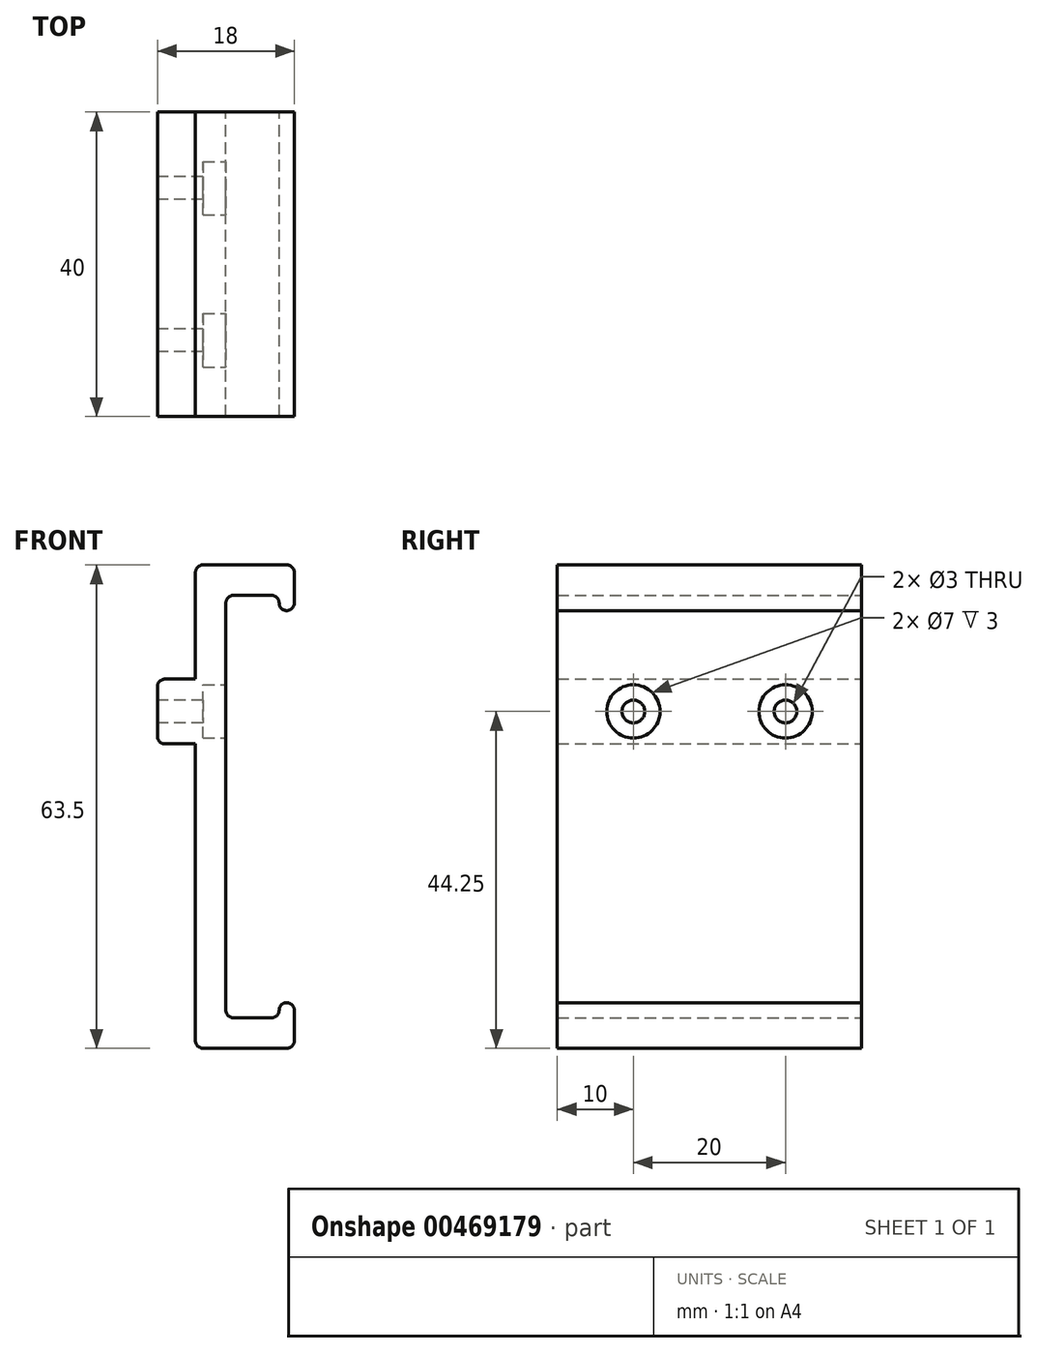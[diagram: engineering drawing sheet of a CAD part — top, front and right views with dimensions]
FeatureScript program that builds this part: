
annotation { "Feature Type Name" : "Feature", "Feature Type Description" : "" }
export const myFeature = defineFeature(function(context is Context, id is Id, definition is map)
    precondition{}
    {
        {
            var Q0;
            Q0=qCreatedBy(makeId("Front.planeOp"),FACE);
            var sketch = newSketch(context, id + "F0", { "sketchPlane" : qUnion([Q0])});
            skLineSegment(sketch, "E0", {"start": v(0, 15) * mm, "end": v(0, 0) * mm});
            skLineSegment(sketch, "E1", {"start": v(0, 0) * mm, "end": v(-5, 0) * mm});
            skLineSegment(sketch, "E2", {"start": v(-5, 0) * mm, "end": v(-5, -8.5) * mm});
            skLineSegment(sketch, "E3", {"start": v(-5, -8.5) * mm, "end": v(0, -8.5) * mm});
            skLineSegment(sketch, "E4", {"start": v(0, -8.5) * mm, "end": v(0, -48.5) * mm});
            skLineSegment(sketch, "E5", {"start": v(0, -48.5) * mm, "end": v(13, -48.5) * mm});
            skLineSegment(sketch, "E6", {"start": v(11, -44.5) * mm, "end": v(4, -44.5) * mm});
            skLineSegment(sketch, "E7", {"start": v(4, -44.5) * mm, "end": v(4, 11) * mm});
            skLineSegment(sketch, "E8", {"start": v(11, 11) * mm, "end": v(4, 11) * mm});
            skLineSegment(sketch, "E9", {"start": v(13, 15) * mm, "end": v(0, 15) * mm});
            skLineSegment(sketch, "E10", {"start": v(13, 9) * mm, "end": v(11, 9) * mm});
            skLineSegment(sketch, "E11", {"start": v(11, 9) * mm, "end": v(11, 11) * mm});
            skLineSegment(sketch, "E12", {"start": v(13, -42.5) * mm, "end": v(11, -42.5) * mm});
            skLineSegment(sketch, "E13", {"start": v(11, -42.5) * mm, "end": v(11, -44.5) * mm});
            skLineSegment(sketch, "E14", {"start": v(13, 15) * mm, "end": v(13, 9) * mm});
            skLineSegment(sketch, "E15", {"start": v(13, -48.5) * mm, "end": v(13, -42.5) * mm});
            skSolve(sketch);
        }
        {
            var Q0;
            Q0=makeQuery(id+"F0.imprint","IMPRINT",FACE,{"disambiguationData":[TD([[makeQuery(id+"F0.imprint","IMPRINT",EDGE,{"derivedFrom":sQuery(id+"F0.wireOp",EDGE,"E0")}),1.0]])]});
            extrude(context, id + "F1", {"entities" : qUnion([Q0]), "depth" : 40 * mm});
        }
        {
            var Q0;
            Q0=makeQuery(id+"F1.opExtrude","SWEPT_FACE",FACE,{"disambiguationData":[OSD([sQuery(id+"F0.wireOp",EDGE,"E2")])]});
            var sketch = newSketch(context, id + "F2", { "sketchPlane" : qUnion([Q0])});
            skCircle(sketch, "E16", {"center": v(10, -4.25) * mm, "radius": 1.5 * mm});
            skPoint(sketch, "E16.centerSnap0", {"position": v(0, -4.25) * mm});
            skCircle(sketch, "E17", {"center": v(30, -4.25) * mm, "radius": 1.5 * mm});
            skSolve(sketch);
        }
        {
            var Q0;
            Q0=makeQuery(id+"F2.imprint","IMPRINT",FACE,{"disambiguationData":[TD([[makeQuery(id+"F2.imprint","IMPRINT",EDGE,{"derivedFrom":sQuery(id+"F2.wireOp",EDGE,"E16")}),1.0]])]});
            var Q1;
            Q1=makeQuery(id+"F2.imprint","IMPRINT",FACE,{"disambiguationData":[TD([[makeQuery(id+"F2.imprint","IMPRINT",EDGE,{"derivedFrom":sQuery(id+"F2.wireOp",EDGE,"E17")}),1.0]])]});
            extrude(context, id + "F3", {"entities" : qUnion([Q0, Q1]), "operationType" : NewBodyOperationType.REMOVE, "oppositeDirection" : true, "depth" : 25 * mm});
        }
        {
            var Q0;
            Q0=makeQuery(id+"F1.opExtrude","SWEPT_FACE",FACE,{"disambiguationData":[OSD([sQuery(id+"F0.wireOp",EDGE,"E7")])]});
            var sketch = newSketch(context, id + "F4", { "sketchPlane" : qUnion([Q0])});
            skCircle(sketch, "E18", {"center": v(-10, -4.25) * mm, "radius": 3.5 * mm});
            skCircle(sketch, "E19", {"center": v(-30, -4.25) * mm, "radius": 3.5 * mm});
            skSolve(sketch);
        }
        {
            var Q0;
            Q0=makeQuery(id+"F1.opExtrude","SWEPT_EDGE",EDGE,{"disambiguationData":[OSD([sQuery(id+"F0.wireOp",EDGE,"E1"),sQuery(id+"F0.wireOp",EDGE,"E2")])]});
            var Q1;
            Q1=makeQuery(id+"F1.opExtrude","SWEPT_EDGE",EDGE,{"disambiguationData":[OSD([sQuery(id+"F0.wireOp",EDGE,"E2"),sQuery(id+"F0.wireOp",EDGE,"E3")])]});
            fillet(context, id + "F5", {"entities" : qUnion([Q0, Q1]), "radius" : 1 * mm, "tangentPropagation" : true, "allowEdgeOverflow" : false});
        }
        {
            var Q0;
            Q0=makeQuery(id+"F4.imprint","IMPRINT",FACE,{"disambiguationData":[TD([[makeQuery(id+"F4.imprint","IMPRINT",EDGE,{"derivedFrom":sQuery(id+"F4.wireOp",EDGE,"E18")}),1.0]])]});
            var Q1;
            Q1=makeQuery(id+"F4.imprint","IMPRINT",FACE,{"disambiguationData":[TD([[makeQuery(id+"F4.imprint","IMPRINT",EDGE,{"derivedFrom":sQuery(id+"F4.wireOp",EDGE,"E19")}),1.0]])]});
            extrude(context, id + "F6", {"entities" : qUnion([Q0, Q1]), "operationType" : NewBodyOperationType.REMOVE, "oppositeDirection" : true, "depth" : 3 * mm});
        }
        {
            var Q0;
            Q0=makeQuery(id+"F1.opExtrude","SWEPT_EDGE",EDGE,{"disambiguationData":[OSD([sQuery(id+"F0.wireOp",EDGE,"E10"),sQuery(id+"F0.wireOp",EDGE,"E14")])]});
            var Q1;
            Q1=makeQuery(id+"F1.opExtrude","SWEPT_EDGE",EDGE,{"disambiguationData":[OSD([sQuery(id+"F0.wireOp",EDGE,"E10"),sQuery(id+"F0.wireOp",EDGE,"E11")])]});
            var Q2;
            Q2=makeQuery(id+"F1.opExtrude","SWEPT_EDGE",EDGE,{"disambiguationData":[OSD([sQuery(id+"F0.wireOp",EDGE,"E9"),sQuery(id+"F0.wireOp",EDGE,"E14")])]});
            var Q3;
            Q3=makeQuery(id+"F1.opExtrude","SWEPT_EDGE",EDGE,{"disambiguationData":[OSD([sQuery(id+"F0.wireOp",EDGE,"E0"),sQuery(id+"F0.wireOp",EDGE,"E9")])]});
            var Q4;
            Q4=makeQuery(id+"F1.opExtrude","SWEPT_EDGE",EDGE,{"disambiguationData":[OSD([sQuery(id+"F0.wireOp",EDGE,"E7"),sQuery(id+"F0.wireOp",EDGE,"E8")])]});
            var Q5;
            Q5=makeQuery(id+"F1.opExtrude","SWEPT_EDGE",EDGE,{"disambiguationData":[OSD([sQuery(id+"F0.wireOp",EDGE,"E4"),sQuery(id+"F0.wireOp",EDGE,"E5")])]});
            var Q6;
            Q6=makeQuery(id+"F1.opExtrude","SWEPT_EDGE",EDGE,{"disambiguationData":[OSD([sQuery(id+"F0.wireOp",EDGE,"E5"),sQuery(id+"F0.wireOp",EDGE,"E15")])]});
            var Q7;
            Q7=makeQuery(id+"F1.opExtrude","SWEPT_EDGE",EDGE,{"disambiguationData":[OSD([sQuery(id+"F0.wireOp",EDGE,"E12"),sQuery(id+"F0.wireOp",EDGE,"E15")])]});
            var Q8;
            Q8=makeQuery(id+"F1.opExtrude","SWEPT_EDGE",EDGE,{"disambiguationData":[OSD([sQuery(id+"F0.wireOp",EDGE,"E6"),sQuery(id+"F0.wireOp",EDGE,"E7")])]});
            var Q9;
            Q9=makeQuery(id+"F1.opExtrude","SWEPT_EDGE",EDGE,{"disambiguationData":[OSD([sQuery(id+"F0.wireOp",EDGE,"E12"),sQuery(id+"F0.wireOp",EDGE,"E13")])]});
            var Q10;
            Q10=makeQuery(id+"F1.opExtrude","SWEPT_EDGE",EDGE,{"disambiguationData":[OSD([sQuery(id+"F0.wireOp",EDGE,"E6"),sQuery(id+"F0.wireOp",EDGE,"E13")])]});
            var Q11;
            Q11=makeQuery(id+"F1.opExtrude","SWEPT_EDGE",EDGE,{"disambiguationData":[OSD([sQuery(id+"F0.wireOp",EDGE,"E8"),sQuery(id+"F0.wireOp",EDGE,"E11")])]});
            fillet(context, id + "F7", {"entities" : qUnion([Q0, Q1, Q2, Q3, Q4, Q5, Q6, Q7, Q8, Q9, Q10, Q11]), "radius" : 1 * mm, "tangentPropagation" : true, "allowEdgeOverflow" : false});
        }
    });
